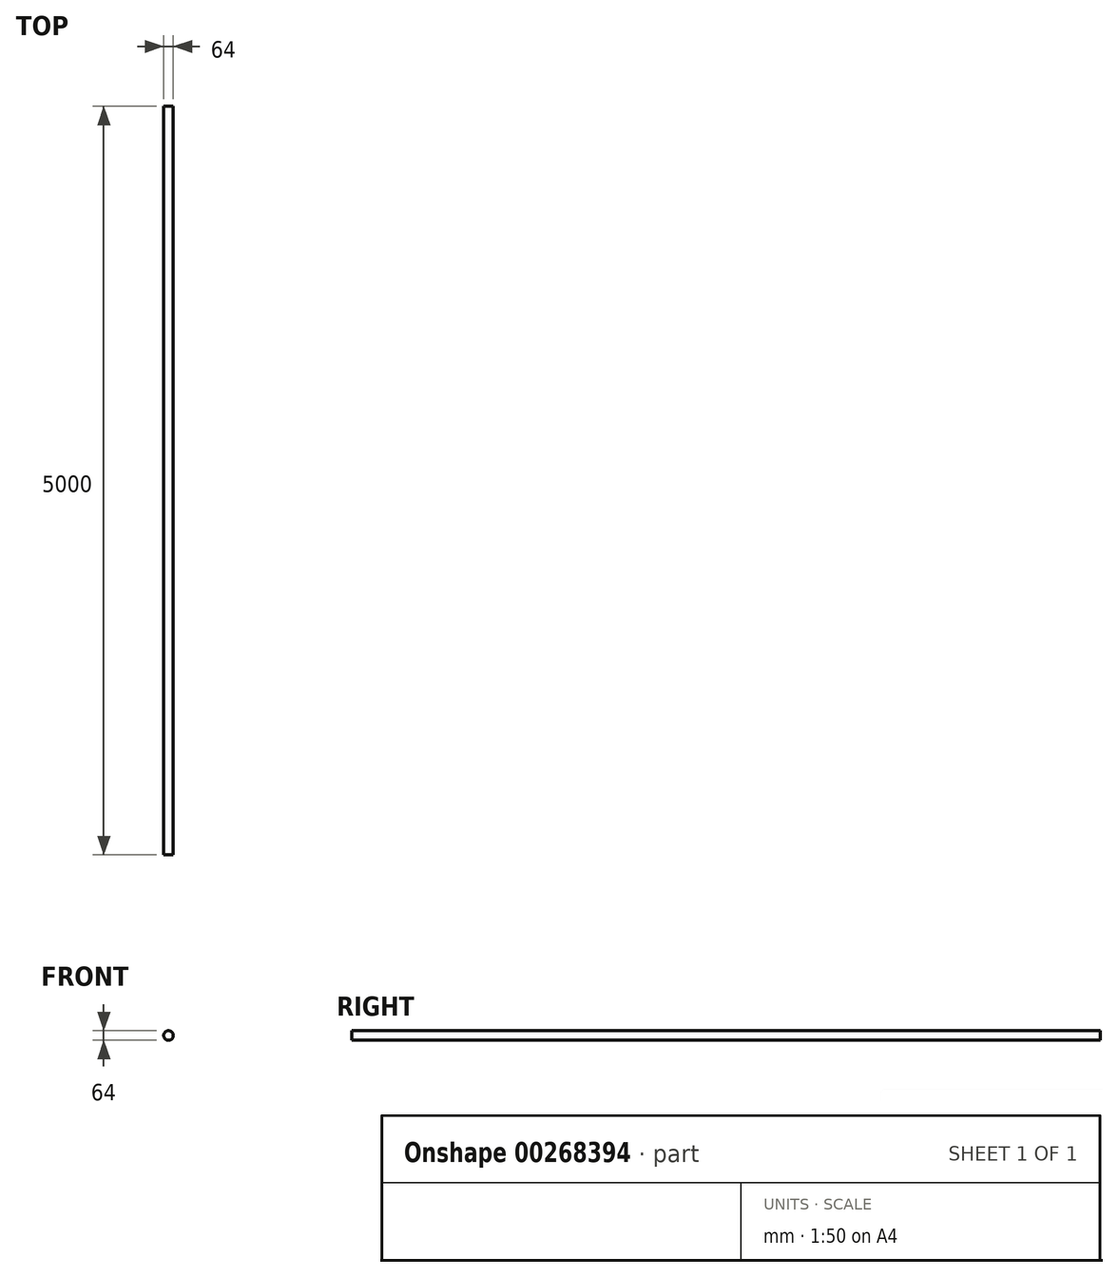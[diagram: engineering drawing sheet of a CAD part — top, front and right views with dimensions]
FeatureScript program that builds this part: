
annotation { "Feature Type Name" : "Feature", "Feature Type Description" : "" }
export const myFeature = defineFeature(function(context is Context, id is Id, definition is map)
    precondition{}
    {
        {
            var Q0;
            Q0=qCreatedBy(makeId("Front.planeOp"),FACE);
            var sketch = newSketch(context, id + "F0", { "sketchPlane" : qUnion([Q0])});
            skCircle(sketch, "E0", {"center": v(0, 0) * mm, "radius": 32 * mm});
            skLineSegment(sketch, "E1", {"start": v(0, 32) * mm, "end": v(0, -32) * mm});
            skSolve(sketch);
        }
        {
            var Q0;
            Q0=makeQuery(id+"F0.imprint","IMPRINT",FACE,{"disambiguationData":[TD([[makeQuery(id+"F0.imprint","IMPRINT",EDGE,{"derivedFrom":sQuery(id+"F0.wireOp",EDGE,"E0")}),1.0]])]});
            extrude(context, id + "F1", {"entities" : qUnion([Q0]), "depth" : 5000 * mm, "offsetDistance" : 25 * mm});
        }
        {
            var Q0;
            Q0=qCreatedBy(makeId("Top.planeOp"),FACE);
            var sketch = newSketch(context, id + "F2", { "sketchPlane" : qUnion([Q0])});
            skLineSegment(sketch, "E2", {"start": v(0, 0) * mm, "end": v(0, 146.63) * mm});
            skSolve(sketch);
        }
    });
